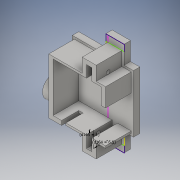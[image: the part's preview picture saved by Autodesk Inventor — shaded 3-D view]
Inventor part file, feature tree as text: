
AUTODESK INVENTOR PART (.ipt)
format: ipt  version: 2016 (Build 200138000, 138)  size: 306,688 bytes
history: native  units: in
note: dims shown in document units (in); Inventor stores cm internally (conversion verified against a paired STEP export)
features: sketch x11, extrude x7, plane x2, hole x1
ambient origin geometry x8: Origin, YZ Plane, XZ Plane, XY Plane, X Axis, Y Axis, Z Axis, Center Point
bodies: Solid1 (feature_tree)
feature tree (21):
  extrude  "Extrusion1"  Depth=0.8976in
  extrude  "Extrusion4"  Depth=0.9016in
  extrude  "Extrusion5"  Depth=0.1004in
  hole  "Hole3"  [1 undecoded]
  plane  "Work Plane1"
  extrude  "Extrusion6"  Depth=0.1713in
  sketch  "Sketch20"  dims[d91=0.2992in d92=0.2165in]
  plane  "Work Plane2"
  sketch  "Sketch21"  dims[d93=0.2165in d95=0.9016in]
  extrude  "Extrusion7"  Depth=0.2165in
  extrude  "Extrusion8"  Depth=0.9016in
  extrude  "Extrusion9"  Depth=0.0787in
  sketch  "Sketch27"  dims[d101=0.0787in d102=0.0787in d103=0.1693in d105=0.0787in d106=0.0394in d107=0.0394in d108=0.0394in d109=0.0394in d110=0.1575in d111=0.0787in d112=0.0787in d113=0.0394in d114=0.9016in d125=0.0984in d130=0.185in d132=0.3543in d133=0.2165in d134=0.4724in d135=0.0in d136=0.0787in d137=0.315in d138=0.0in d139=0.0787in d144=0.0394in d145=0.7461in d146=0.0394in d147=0.07in d148=0.2362in d149=0.119in d150=0.0787in d151=0.5635in d152=0.315in d153=0.8108in d156=0.2717in d157=0.2323in d158=0.2756in d159=0.3937in d160=0.1575in d161=0.0in d164=0.2559in d165=0.0394in d166=0.1575in d167=0.0in d173=0.0906in d174=0.0in d177=0.0394in d178=0.0394in d179=0.0394in d180=0.1181in d181=0.0394in d182=0.0394in d183=0.0394in d184=0.0394in d185=0.1181in d186=0.0394in d187=0.1575in d188=0.1181in d189=0.3937in d190=0.0in d26=0.0394in d27=0.0394in]
  sketch  "Sketch1"  dims[d2=0.1181in d3=0.0in d6=0.8976in d9=0.357in d10=0.7139in]
  sketch  "Sketch12"  dims[d11=0.0787in d12=0.0787in d13=0.0787in d14=0.0787in d82=0.9016in d83=0.8858in]
  sketch  "Sketch14"  dims[d85=0.1004in d86=0.1004in]
  sketch  "Sketch17"  dims[d87=0.6142in d88=0.6142in]
  sketch  "Sketch18"  dims[d89=0.1713in d90=0.1713in]
  sketch  "Sketch22"  dims[d97=0.0787in d98=0.0787in]
  sketch  "Sketch25"  dims[d99=0.0787in]
  sketch  "Sketch26"  dims[d100=0.0787in]
note: 1 required parameter value undecoded (feature->parameter linkage not recoverable at this tier; creation-order binding heuristic only, values carry confidence <= 0.55)
